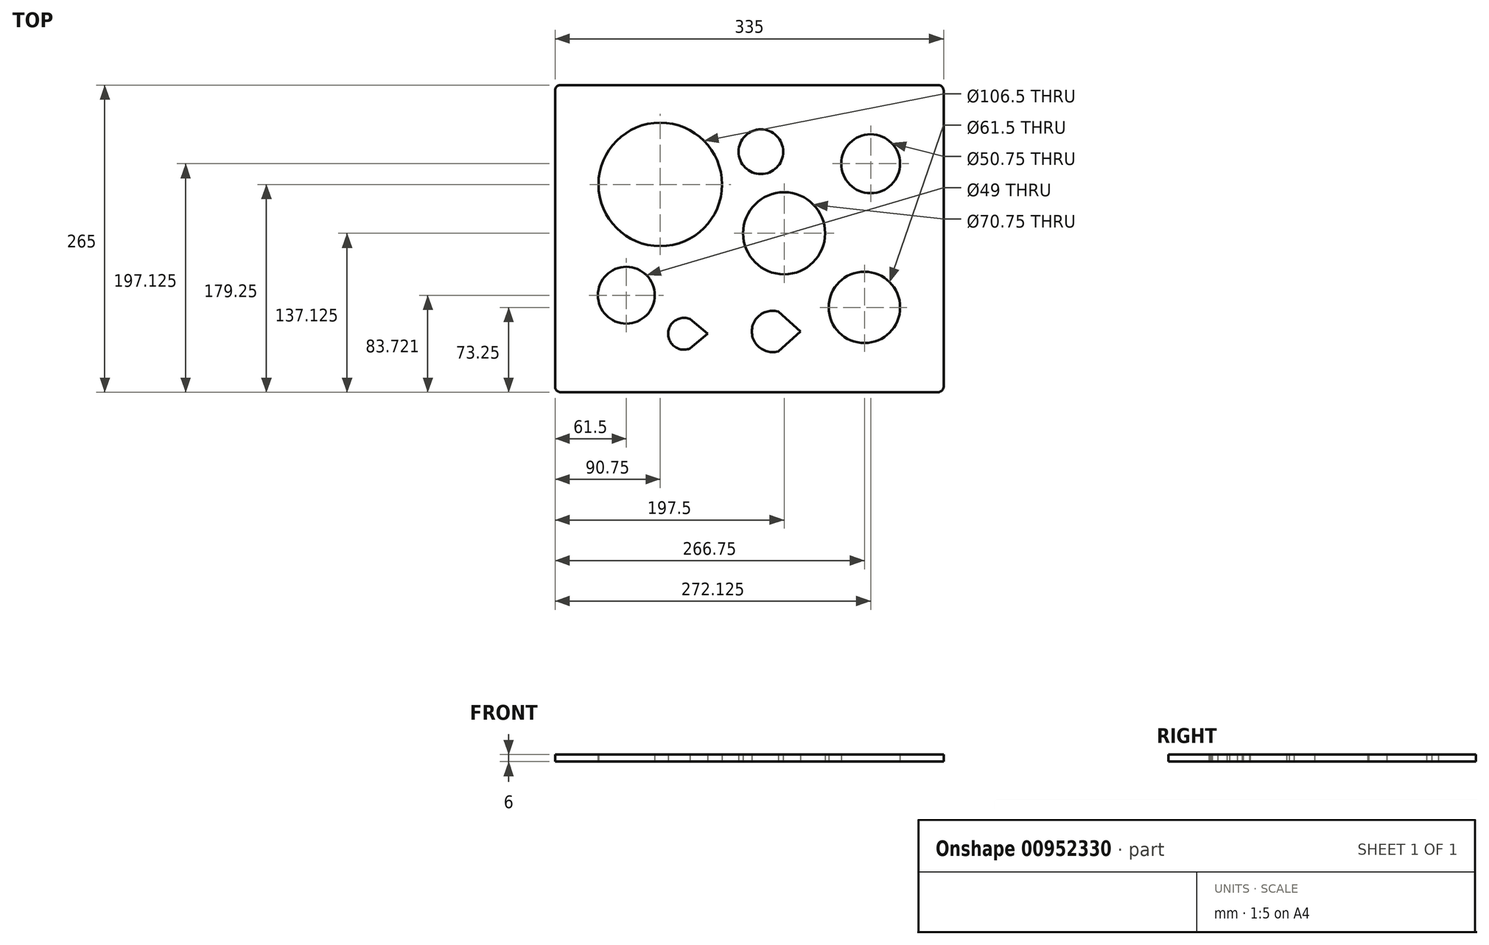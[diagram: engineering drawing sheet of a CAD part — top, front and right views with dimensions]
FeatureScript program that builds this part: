
annotation { "Feature Type Name" : "Feature", "Feature Type Description" : "" }
export const myFeature = defineFeature(function(context is Context, id is Id, definition is map)
    precondition{}
    {
        {
            var Q0;
            Q0=qCreatedBy(makeId("Top.planeOp"),FACE);
            var sketch = newSketch(context, id + "F0", { "sketchPlane" : qUnion([Q0])});
            skLineSegment(sketch, "E0.bottom", {"start": v(167.5, -132.5) * mm, "end": v(-167.5, -132.5) * mm});
            skLineSegment(sketch, "E0.top", {"start": v(167.5, 132.5) * mm, "end": v(-167.5, 132.5) * mm});
            skLineSegment(sketch, "E0.left", {"start": v(167.5, -132.5) * mm, "end": v(167.5, 132.5) * mm});
            skLineSegment(sketch, "E0.right", {"start": v(-167.5, -132.5) * mm, "end": v(-167.5, 132.5) * mm});
            skPoint(sketch, "E0.middle", {"position": v(0, 0) * mm});
            skLineSegment(sketch, "E1.bottom", {"start": v(130, -100) * mm, "end": v(-130, -100) * mm, "construction": true});
            skLineSegment(sketch, "E1.top", {"start": v(130, 100) * mm, "end": v(-130, 100) * mm, "construction": true});
            skLineSegment(sketch, "E1.left", {"start": v(130, -100) * mm, "end": v(130, 100) * mm, "construction": true});
            skLineSegment(sketch, "E1.right", {"start": v(-130, -100) * mm, "end": v(-130, 100) * mm, "construction": true});
            skCircle(sketch, "E2", {"center": v(-76.75, 46.75) * mm, "radius": 53.25 * mm});
            skCircle(sketch, "E3", {"center": v(99.25, -59.25) * mm, "radius": 30.75 * mm});
            skCircle(sketch, "E4", {"center": v(104.62, 64.63) * mm, "radius": 25.38 * mm});
            skCircle(sketch, "E5", {"center": v(10, 75) * mm, "radius": 19.25 * mm});
            skCircle(sketch, "E6", {"center": v(-106, -48.78) * mm, "radius": 24.5 * mm});
            skArc(sketch, "E7", {"start": v(-51.28, -69.22) * mm, "mid": v(-70, -82) * mm, "end": v(-51.28, -94.78) * mm});
            skLineSegment(sketch, "E8", {"start": v(-51.28, -69.22) * mm, "end": v(-51.28, -94.78) * mm, "construction": true});
            skLineSegment(sketch, "E9", {"start": v(-51.28, -82) * mm, "end": v(-36, -82) * mm, "construction": true});
            skLineSegment(sketch, "E10", {"start": v(-51.28, -69.22) * mm, "end": v(-36, -82) * mm});
            skLineSegment(sketch, "E11", {"start": v(-51.28, -94.78) * mm, "end": v(-36, -82) * mm});
            skArc(sketch, "E12", {"start": v(25, -62.9) * mm, "mid": v(2.17, -80) * mm, "end": v(25, -97.1) * mm});
            skLineSegment(sketch, "E13", {"start": v(25, -62.9) * mm, "end": v(25, -97.1) * mm, "construction": true});
            skLineSegment(sketch, "E14", {"start": v(25, -80) * mm, "end": v(44.17, -80) * mm, "construction": true});
            skLineSegment(sketch, "E15", {"start": v(25, -62.9) * mm, "end": v(44.17, -80) * mm});
            skLineSegment(sketch, "E16", {"start": v(25, -97.1) * mm, "end": v(44.17, -80) * mm});
            skArc(sketch, "E17", {"start": v(45, -37.33) * mm, "mid": v(26.38, -50) * mm, "end": v(45, -62.67) * mm, "construction": true});
            skLineSegment(sketch, "E18", {"start": v(45, -37.33) * mm, "end": v(45, -62.67) * mm, "construction": true});
            skLineSegment(sketch, "E19", {"start": v(45, -50) * mm, "end": v(59.38, -50) * mm, "construction": true});
            skLineSegment(sketch, "E20", {"start": v(45, -37.33) * mm, "end": v(59.38, -50) * mm, "construction": true});
            skLineSegment(sketch, "E21", {"start": v(45, -62.67) * mm, "end": v(59.38, -50) * mm, "construction": true});
            skArc(sketch, "E22", {"start": v(-35, -38.95) * mm, "mid": v(-52.13, -50) * mm, "end": v(-35, -61.05) * mm, "construction": true});
            skLineSegment(sketch, "E23", {"start": v(-35, -38.95) * mm, "end": v(-35, -61.05) * mm, "construction": true});
            skLineSegment(sketch, "E24", {"start": v(-35, -50) * mm, "end": v(-23.13, -50) * mm, "construction": true});
            skLineSegment(sketch, "E25", {"start": v(-35, -38.95) * mm, "end": v(-23.13, -50) * mm, "construction": true});
            skLineSegment(sketch, "E26", {"start": v(-35, -61.05) * mm, "end": v(-23.13, -50) * mm, "construction": true});
            skCircle(sketch, "E27", {"center": v(30, 4.63) * mm, "radius": 35.38 * mm});
            skSolve(sketch);
        }
        {
            var Q0;
            Q0=makeQuery(id+"F0.imprint","IMPRINT",FACE,{"disambiguationData":[TD([[makeQuery(id+"F0.imprint","IMPRINT",EDGE,{"derivedFrom":sQuery(id+"F0.wireOp",EDGE,"E0.bottom")}),-1.0]])]});
            extrude(context, id + "F1", {"entities" : qUnion([Q0]), "depth" : 6 * mm, "offsetDistance" : 25 * mm});
        }
        {
            var Q0;
            Q0=makeQuery(id+"F1.opExtrude","SWEPT_EDGE",EDGE,{"disambiguationData":[OSD([sQuery(id+"F0.wireOp",EDGE,"E0.top"),sQuery(id+"F0.wireOp",EDGE,"E0.right")])]});
            var Q1;
            Q1=makeQuery(id+"F1.opExtrude","SWEPT_EDGE",EDGE,{"disambiguationData":[OSD([sQuery(id+"F0.wireOp",EDGE,"E0.top"),sQuery(id+"F0.wireOp",EDGE,"E0.left")])]});
            var Q2;
            Q2=makeQuery(id+"F1.opExtrude","SWEPT_EDGE",EDGE,{"disambiguationData":[OSD([sQuery(id+"F0.wireOp",EDGE,"E0.bottom"),sQuery(id+"F0.wireOp",EDGE,"E0.left")])]});
            var Q3;
            Q3=makeQuery(id+"F1.opExtrude","SWEPT_EDGE",EDGE,{"disambiguationData":[OSD([sQuery(id+"F0.wireOp",EDGE,"E0.bottom"),sQuery(id+"F0.wireOp",EDGE,"E0.right")])]});
            fillet(context, id + "F2", {"entities" : qUnion([Q0, Q1, Q2, Q3]), "radius" : 5 * mm, "tangentPropagation" : true, "allowEdgeOverflow" : false});
        }
    });
